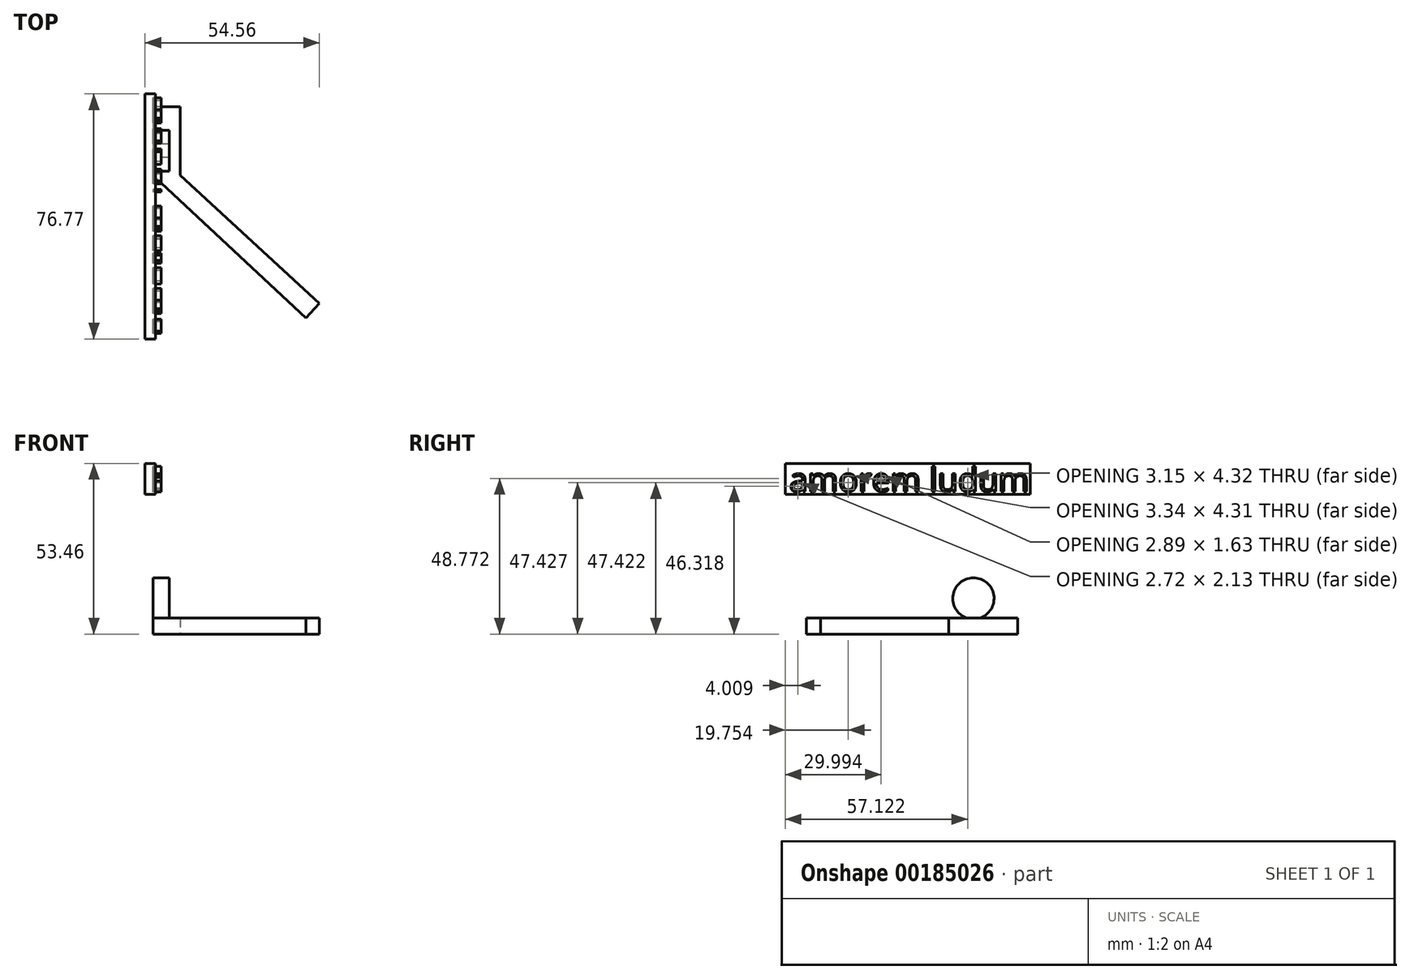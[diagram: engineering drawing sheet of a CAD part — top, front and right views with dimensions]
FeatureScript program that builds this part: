
annotation { "Feature Type Name" : "Feature", "Feature Type Description" : "" }
export const myFeature = defineFeature(function(context is Context, id is Id, definition is map)
    precondition{}
    {
        {
            var Q0;
            Q0=qCreatedBy(makeId("Right.planeOp"),FACE);
            var sketch = newSketch(context, id + "F0", { "sketchPlane" : qUnion([Q0])});
            skCircle(sketch, "E0", {"center": v(15.53, 11.19) * mm, "radius": 6.46 * mm});
            skPoint(sketch, "E0.first.point", {"position": v(19.84, 15.99) * mm});
            skPoint(sketch, "E0.second.point", {"position": v(9.11, 10.47) * mm});
            skPoint(sketch, "E0.third.point", {"position": v(21.98, 11.27) * mm});
            skSolve(sketch);
        }
        {
            var Q0;
            Q0=makeQuery(id+"F0.imprint","IMPRINT",FACE,{"disambiguationData":[TD([[makeQuery(id+"F0.imprint","IMPRINT",EDGE,{"derivedFrom":sQuery(id+"F0.wireOp",EDGE,"E0")}),1.0]])]});
            extrude(context, id + "F1", {"entities" : qUnion([Q0]), "depth" : 5.08 * mm});
        }
        {
            var Q0;
            Q0=qCreatedBy(makeId("Top.planeOp"),FACE);
            var sketch = newSketch(context, id + "F2", { "sketchPlane" : qUnion([Q0])});
            skLineSegment(sketch, "E1", {"start": v(8.53, 7.8) * mm, "end": v(8.53, 29.38) * mm});
            skLineSegment(sketch, "E2", {"start": v(8.53, 29.38) * mm, "end": v(0, 29.38) * mm});
            skLineSegment(sketch, "E3", {"start": v(0, 29.38) * mm, "end": v(0, 7.87) * mm});
            skLineSegment(sketch, "E4", {"start": v(0, 7.87) * mm, "end": v(47.82, -36.79) * mm});
            skLineSegment(sketch, "E5", {"start": v(47.82, -36.79) * mm, "end": v(52.02, -32.3) * mm});
            skLineSegment(sketch, "E6", {"start": v(52.02, -32.3) * mm, "end": v(8.53, 7.8) * mm});
            skSolve(sketch);
        }
        {
            var Q0;
            Q0=makeQuery(id+"F2.imprint","IMPRINT",FACE,{"disambiguationData":[TD([[makeQuery(id+"F2.imprint","IMPRINT",EDGE,{"derivedFrom":sQuery(id+"F2.wireOp",EDGE,"E1")}),1.0]])]});
            extrude(context, id + "F3", {"entities" : qUnion([Q0]), "operationType" : NewBodyOperationType.ADD, "depth" : 5.08 * mm});
        }
        {
            var Q0;
            Q0=qCreatedBy(makeId("Right.planeOp"),FACE);
            var sketch = newSketch(context, id + "F4", { "sketchPlane" : qUnion([Q0])});
            skText(sketch, "E7", { "text": "\namorem ludum", "fontName": "OpenSans-Regular.ttf"});
            const initialGuessF4  = {"E7": [-0.0421, 0.0587, 1, 0, 0.00743]};
            skSetInitialGuess(sketch, initialGuessF4);
            skSolve(sketch);
        }
        {
            var Q0;
            Q0 = qSketchRegion(id + "F4", true);
            extrude(context, id + "F5", {"entities" : qUnion([Q0]), "depth" : 2.54 * mm});
        }
        {
            var Q0;
            Q0=qCreatedBy(makeId("Right.planeOp"),FACE);
            var sketch = newSketch(context, id + "F6", { "sketchPlane" : qUnion([Q0])});
            skLineSegment(sketch, "E8.bottom", {"start": v(33.37, 43.82) * mm, "end": v(-43.4, 43.82) * mm});
            skLineSegment(sketch, "E8.top", {"start": v(33.37, 53.46) * mm, "end": v(-43.4, 53.46) * mm});
            skLineSegment(sketch, "E8.left", {"start": v(33.37, 43.82) * mm, "end": v(33.37, 53.46) * mm});
            skLineSegment(sketch, "E8.right", {"start": v(-43.4, 43.82) * mm, "end": v(-43.4, 53.46) * mm});
            skSolve(sketch);
        }
        {
            var Q0;
            Q0=makeQuery(id+"F6.imprint","IMPRINT",FACE,{"disambiguationData":[TD([[makeQuery(id+"F6.imprint","IMPRINT",EDGE,{"derivedFrom":sQuery(id+"F6.wireOp",EDGE,"E8.bottom")}),-1.0]])]});
            extrude(context, id + "F7", {"entities" : qUnion([Q0]), "oppositeDirection" : true, "depth" : 2.54 * mm, "hasSecondDirection" : true, "secondDirectionOppositeDirection" : false, "secondDirectionDepth" : 0.76 * mm});
        }
    });
